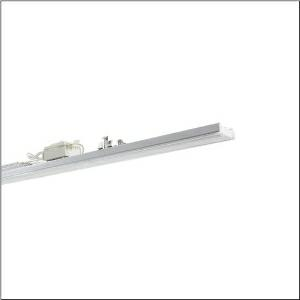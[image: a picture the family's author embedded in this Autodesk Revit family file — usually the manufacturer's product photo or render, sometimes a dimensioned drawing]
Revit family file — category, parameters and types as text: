
# Revit family: licross_21_recessed_mo_52tl12dv4fxgd
name_source: partatom
category: Lighting Fixtures
units: mm (PartAtom-declared; Revit-internal decimal feet)

## family parameters
Cut with Voids When Loaded = No
Host = Face
Light Source = No
Part Type = Normal
Room Calculation Point = No
Round Connector Dimension = Use Diameter
Shared = No

## types (1)
- --- (1 x LED, 15420 lm, 85.3 W, 4000K)
    Apparent Load = 85 VA
    CIE Flux Codes = 72 92 99 100 100
    Color Rendering = 80
    Color Temperature = 4000K
    Default Elevation = 1800 mm
    Description = Licross 21 Recessed MO, luminaire insert, of sheet steel, galvanised, coil coated, white, length: 2.250mm, width: 66mm, height: 67mm, LED rated luminous flux: 15.420lm, light colour: 840, SDCM (Standard Deviation of Colour Matching)MacAdam ≤ 3 SDCM (initial), control gear: DALI 2 (for two DALI lines), with plug, 6-pole, with phase selection, mains connection: 220..240V, AC/DC, 0/50..60Hz, rated input power: 85W, without changeover relay, for emergency light function, for central battery installations according to EN 60598-2-22, internal wiring halogen-free, primary optical cover: cover, of PMMA, light emission: direct distribution, primary light characteristic: symmetric, protection rating (complete): IP40, insulation class (complete): insulation class I (protective earthing), certification: CE, ENEC, VDE, UKCA, protection symbol: D if used in an environment without relevant dust loads with corresponding accessories, impact resistance: IK06, permissible ambient temperature for indoor applications: -25..+35°C, standard: EN 60598-2-22, corresponds to IFS (International Featured Standards) requirements for safety and quality in the food industry, reducing of maximum allowable ambient temperature of 5°C with ceiling mounting, LABS conformity tested according to VDMA 24364:2018-05, The light source and the operating device comply with the requirements of the Ecodesign Regulation (EU) 2019/2020 and are replaceable in accordance with this regulation, packaging unit: 1 piece
    Height = 58 mm
    Lamp = 1 x LED
    Lamp Light Flux = 15420 lm
    Lamp Power = 85.3 W
    Lamp count = 1
    Length = 2250 mm
    Luminous efficacy = 181 lm/W
    Manufacturer = Siteco
    ModVariant = No
    Model = 52TL12DV4FXGD
    Mounting Place = Ceiling
    Mounting Type = Pendant
    Number of Poles = 1
    OnlyDefault = Yes
    Power Factor = 1
    Product Name = Licross 21 Recessed MO
    Product group = luminaire insert | ceiling pendant
    ProductGroupID = 901
    Protection Class = Protection class I
    Protection Degree = IP 40
    RLX_Detail_Level = 1
    RLX_Emergency_Light_Flux = 0 lm
    RLX_Emergency_Type = 0
    RLX_Emergency_Type_DB = No
    RlxData = <blob elided: 30333 chars, md5=dab8e93e>
    Socket = socket
    Standby Power = 0 W
    System Light Flux = 15420 lm
    System Power = 85 W
    Type Comments = : AC-mode, luminous flux: 100 % | dim-lin: 254 | 390 mA
    Type Image = l_1296930.jpg
    URL = http://relux.com
    VarID = @adj_113181
    Voltage = 0 V
    Weight = 0.00 kg
    Width = 66 mm

## geometry (parser evidence)
native form markers: Blend x4, Sweep x9
no freeform markers — native parametric forms only
